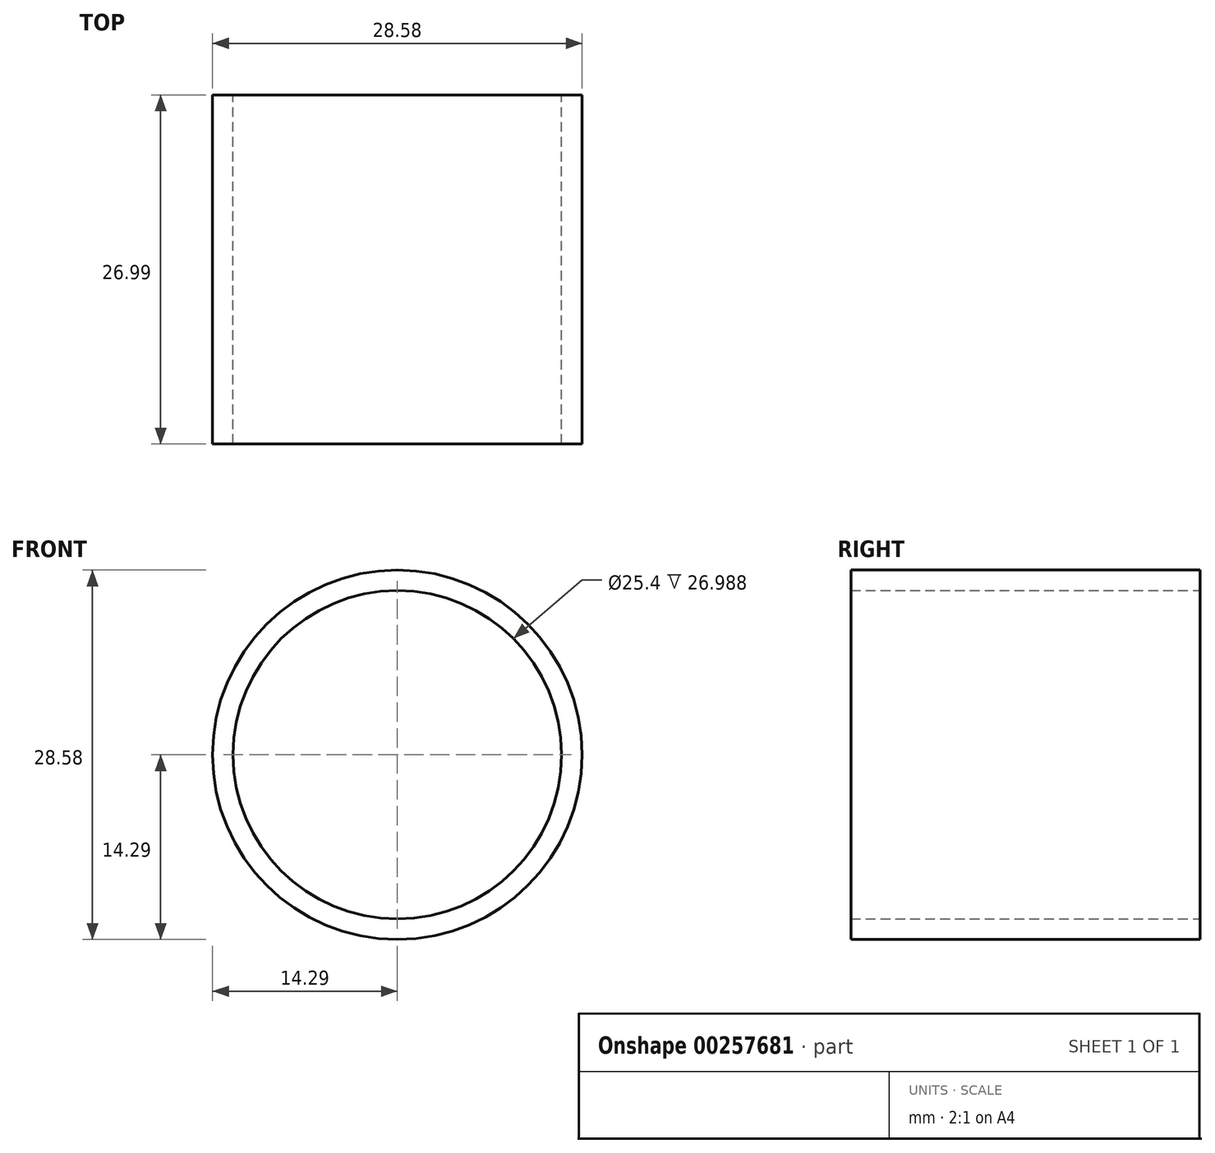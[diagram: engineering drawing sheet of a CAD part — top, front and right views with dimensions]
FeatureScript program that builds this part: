
annotation { "Feature Type Name" : "Feature", "Feature Type Description" : "" }
export const myFeature = defineFeature(function(context is Context, id is Id, definition is map)
    precondition{}
    {
        {
            var Q0;
            Q0=qCreatedBy(makeId("Front.planeOp"),FACE);
            var sketch = newSketch(context, id + "F0", { "sketchPlane" : qUnion([Q0])});
            skCircle(sketch, "E0", {"center": v(0, 0) * mm, "radius": 12.7 * mm});
            skCircle(sketch, "E1", {"center": v(0, 0) * mm, "radius": 14.29 * mm});
            skSolve(sketch);
        }
        {
            var Q0;
            Q0=makeQuery(id+"F0.imprint","IMPRINT",FACE,{"disambiguationData":[TD([[makeQuery(id+"F0.imprint","IMPRINT",EDGE,{"derivedFrom":sQuery(id+"F0.wireOp",EDGE,"E0")}),-1.0]])]});
            extrude(context, id + "F1", {"entities" : qUnion([Q0]), "depth" : 26.99 * mm});
        }
    });
